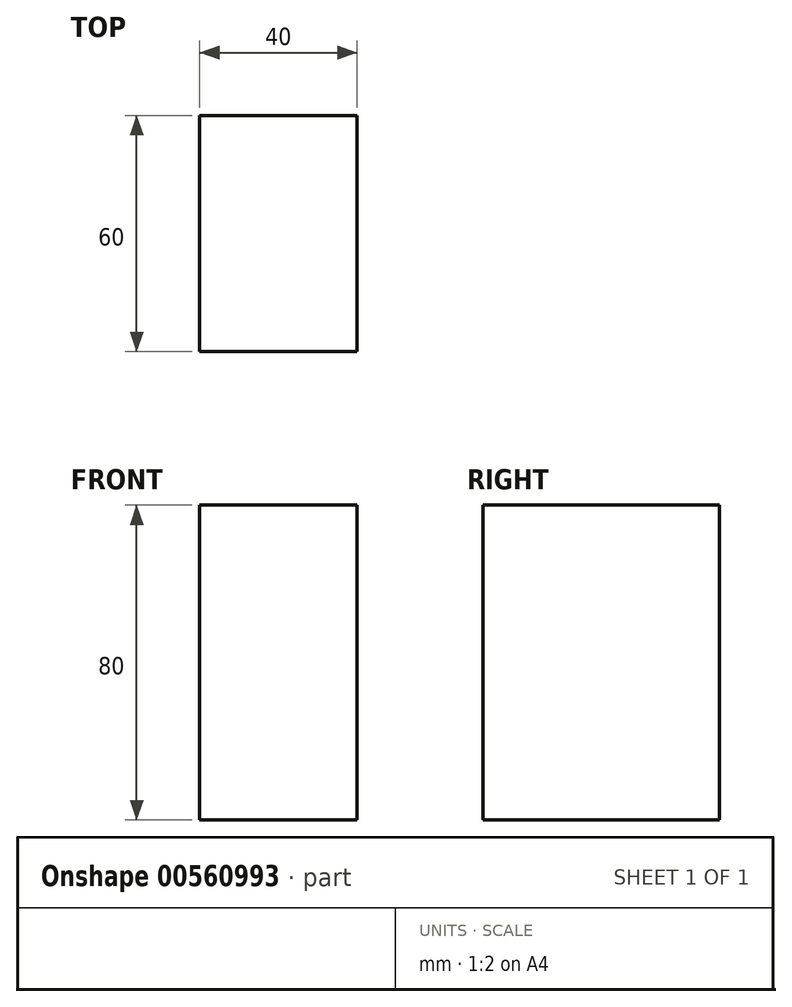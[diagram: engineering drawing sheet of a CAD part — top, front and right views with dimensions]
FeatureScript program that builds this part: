
annotation { "Feature Type Name" : "Feature", "Feature Type Description" : "" }
export const myFeature = defineFeature(function(context is Context, id is Id, definition is map)
    precondition{}
    {
        {
            var Q0;
            Q0=qCreatedBy(makeId("Top.planeOp"),FACE);
            var sketch = newSketch(context, id + "F0", { "sketchPlane" : qUnion([Q0])});
            skLineSegment(sketch, "E0.bottom", {"start": v(0, 0) * mm, "end": v(40, 0) * mm});
            skLineSegment(sketch, "E0.top", {"start": v(0, 60) * mm, "end": v(40, 60) * mm});
            skLineSegment(sketch, "E0.left", {"start": v(0, 0) * mm, "end": v(0, 60) * mm});
            skLineSegment(sketch, "E0.right", {"start": v(40, 0) * mm, "end": v(40, 60) * mm});
            skSolve(sketch);
        }
        {
            var Q0;
            Q0 = qSketchRegion(id + "F0", true);
            extrude(context, id + "F1", {"entities" : qUnion([Q0]), "depth" : 80 * mm, "offsetDistance" : 25 * mm});
        }
    });
